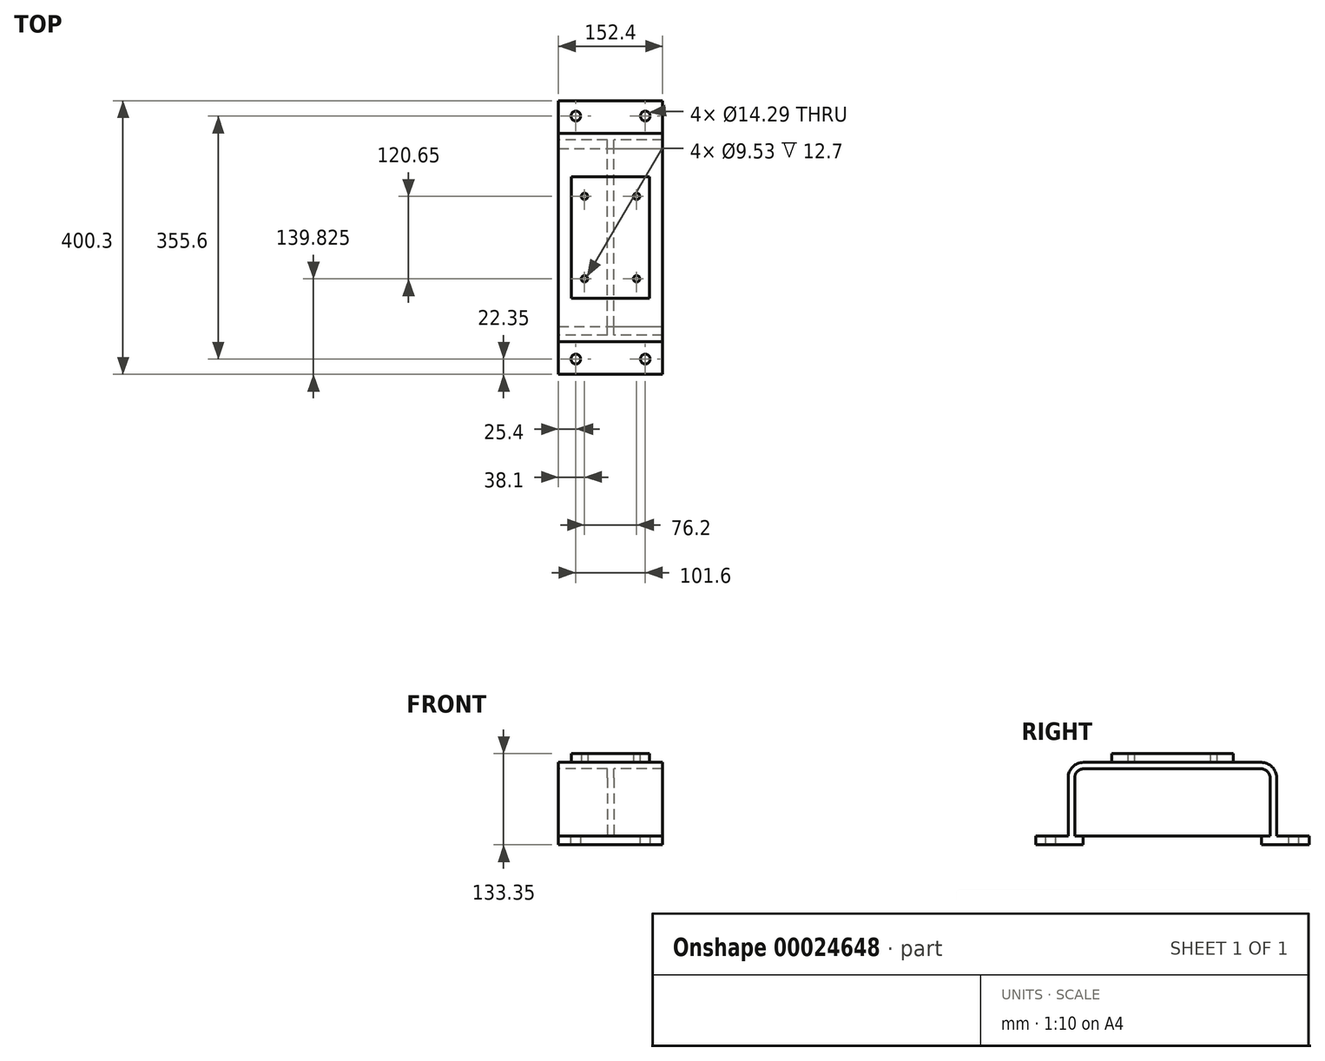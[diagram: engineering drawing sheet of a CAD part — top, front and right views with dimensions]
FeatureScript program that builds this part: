
annotation { "Feature Type Name" : "Feature", "Feature Type Description" : "" }
export const myFeature = defineFeature(function(context is Context, id is Id, definition is map)
    precondition{}
    {
        {
            var Q0;
            Q0=qCreatedBy(makeId("Top.planeOp"),FACE);
            var sketch = newSketch(context, id + "F0", { "sketchPlane" : qUnion([Q0])});
            skLineSegment(sketch, "E0", {"start": v(-115.53, 0) * mm, "end": v(98.36, 0) * mm, "construction": true});
            skLineSegment(sketch, "E1", {"start": v(0, 105.7) * mm, "end": v(0, -103.2) * mm, "construction": true});
            skLineSegment(sketch, "E2.0", {"start": v(-76.2, 105.7) * mm, "end": v(-76.2, -200.15) * mm, "construction": true});
            skLineSegment(sketch, "E3.0", {"start": v(-115.53, -200.15) * mm, "end": v(98.36, -200.15) * mm, "construction": true});
            skLineSegment(sketch, "E4.bottom", {"start": v(-76.2, -200.15) * mm, "end": v(76.2, -200.15) * mm});
            skLineSegment(sketch, "E4.top", {"start": v(-76.2, -130.3) * mm, "end": v(76.2, -130.3) * mm});
            skLineSegment(sketch, "E4.left", {"start": v(-76.2, -200.15) * mm, "end": v(-76.2, -130.3) * mm});
            skLineSegment(sketch, "E4.right", {"start": v(76.2, -200.15) * mm, "end": v(76.2, -130.3) * mm});
            skLineSegment(sketch, "E5.0", {"start": v(-115.53, -177.8) * mm, "end": v(98.36, -177.8) * mm, "construction": true});
            skLineSegment(sketch, "E6", {"start": v(0, -130.3) * mm, "end": v(0, -200.15) * mm, "construction": true});
            skLineSegment(sketch, "E7.0", {"start": v(-50.8, -130.3) * mm, "end": v(-50.8, -200.15) * mm, "construction": true});
            skCircle(sketch, "E8", {"center": v(-50.8, -177.8) * mm, "radius": 7.14 * mm});
            skCircle(sketch, "E9.MirrorC", {"center": v(50.8, -177.8) * mm, "radius": 7.14 * mm});
            skCircle(sketch, "E10.MirrorC", {"center": v(50.8, 177.8) * mm, "radius": 7.14 * mm});
            skCircle(sketch, "E11.MirrorC", {"center": v(-50.8, 177.8) * mm, "radius": 7.14 * mm});
            skLineSegment(sketch, "E12.MirrorCS", {"start": v(0, 130.3) * mm, "end": v(0, 200.15) * mm, "construction": true});
            skLineSegment(sketch, "E13.MirrorCS", {"start": v(-50.8, 130.3) * mm, "end": v(-50.8, 200.15) * mm, "construction": true});
            skLineSegment(sketch, "E14.MirrorCS", {"start": v(-76.2, 200.15) * mm, "end": v(76.2, 200.15) * mm});
            skLineSegment(sketch, "E15.MirrorCS", {"start": v(-76.2, 130.3) * mm, "end": v(76.2, 130.3) * mm});
            skLineSegment(sketch, "E16.MirrorCS", {"start": v(-76.2, 200.15) * mm, "end": v(-76.2, 130.3) * mm});
            skLineSegment(sketch, "E17.MirrorCS", {"start": v(76.2, 200.15) * mm, "end": v(76.2, 130.3) * mm});
            skSolve(sketch);
        }
        {
            var Q0;
            Q0 = qSketchRegion(id + "F0", true);
            extrude(context, id + "F1", {"entities" : qUnion([Q0]), "oppositeDirection" : true, "depth" : 12.7 * mm});
        }
        {
            var Q0;
            Q0=qCreatedBy(makeId("Right.planeOp"),FACE);
            var sketch = newSketch(context, id + "F2", { "sketchPlane" : qUnion([Q0])});
            skLineSegment(sketch, "E18", {"start": v(0, 198.33) * mm, "end": v(0, -186.22) * mm, "construction": true});
            skLineSegment(sketch, "E19", {"start": v(0, 0) * mm, "end": v(-335.1, 0) * mm, "construction": true});
            skLineSegment(sketch, "E20.0", {"start": v(-152.4, 85.6) * mm, "end": v(-152.4, 0) * mm});
            skLineSegment(sketch, "E21.0", {"start": v(0, 107.95) * mm, "end": v(-130.05, 107.95) * mm});
            skPoint(sketch, "E22.visualSharp", {"position": v(-152.4, 107.95) * mm});
            skArc(sketch, "E22.filletArc", {"start": v(-130.05, 107.95) * mm, "mid": v(-145.85, 101.4) * mm, "end": v(-152.4, 85.6) * mm});
            skLineSegment(sketch, "E23.0", {"start": v(-142.87, 85.6) * mm, "end": v(-142.87, 0) * mm});
            skArc(sketch, "E23.1", {"start": v(-130.05, 98.43) * mm, "mid": v(-139.12, 94.67) * mm, "end": v(-142.87, 85.6) * mm});
            skLineSegment(sketch, "E23.2", {"start": v(0, 98.43) * mm, "end": v(-130.05, 98.42) * mm});
            skLineSegment(sketch, "E24", {"start": v(-152.4, 0) * mm, "end": v(-142.87, 0) * mm});
            skLineSegment(sketch, "E25.MirrorCS", {"start": v(152.4, 0) * mm, "end": v(142.87, 0) * mm});
            skArc(sketch, "E26.MirrorCS", {"start": v(130.05, 98.43) * mm, "mid": v(139.12, 94.67) * mm, "end": v(142.87, 85.6) * mm});
            skLineSegment(sketch, "E27.MirrorCS", {"start": v(142.87, 85.6) * mm, "end": v(142.87, 0) * mm});
            skArc(sketch, "E28.MirrorCS", {"start": v(130.05, 107.95) * mm, "mid": v(145.85, 101.4) * mm, "end": v(152.4, 85.6) * mm});
            skLineSegment(sketch, "E29.MirrorCS", {"start": v(0, 107.95) * mm, "end": v(130.05, 107.95) * mm});
            skLineSegment(sketch, "E30.MirrorCS", {"start": v(152.4, 85.6) * mm, "end": v(152.4, 0) * mm});
            skPoint(sketch, "E31.MirrorP", {"position": v(152.4, 107.95) * mm});
            skLineSegment(sketch, "E32.MirrorCS", {"start": v(0, 98.43) * mm, "end": v(130.05, 98.42) * mm});
            skSolve(sketch);
        }
        {
            var Q0;
            Q0 = qSketchRegion(id + "F2", true);
            extrude(context, id + "F3", {"entities" : qUnion([Q0]), "endBound" : BoundingType.SYMMETRIC, "depth" : 152.4 * mm});
        }
        {
            var Q0;
            Q0=qCreatedBy(makeId("Front.planeOp"),FACE);
            var sketch = newSketch(context, id + "F4", { "sketchPlane" : qUnion([Q0])});
            skLineSegment(sketch, "E33", {"start": v(0, 0) * mm, "end": v(0, 134.5) * mm, "construction": true});
            skLineSegment(sketch, "E34.0", {"start": v(-4.76, 0) * mm, "end": v(-4.76, 98.42) * mm});
            skLineSegment(sketch, "E35.0", {"start": v(76.2, 98.42) * mm, "end": v(-76.2, 98.42) * mm});
            skLineSegment(sketch, "E36.MirrorCS", {"start": v(4.76, 0) * mm, "end": v(4.76, 98.42) * mm});
            skLineSegment(sketch, "E37.0", {"start": v(-76.2, 0) * mm, "end": v(76.2, 0) * mm});
            skSolve(sketch);
        }
        {
            var Q0;
            Q0 = qSketchRegion(id + "F4", true);
            var Q1;
            Q1=makeQuery(id+"F3.opExtrude","SWEPT_FACE",FACE,{"disambiguationData":[OSD([sQuery(id+"F2.wireOp",EDGE,"E23.0")])]});
            var Q2;
            Q2=makeQuery(id+"F3.opExtrude","SWEPT_FACE",FACE,{"disambiguationData":[OSD([sQuery(id+"F2.wireOp",EDGE,"E27.MirrorCS")])]});
            extrude(context, id + "F5", {"entities" : qUnion([Q0]), "endBound" : BoundingType.UP_TO_SURFACE, "endBoundEntityFace" : qUnion([Q1]), "depth" : 25.4 * mm, "hasSecondDirection" : true, "secondDirectionBound" : SecondDirectionBoundingType.UP_TO_SURFACE, "secondDirectionOppositeDirection" : true, "secondDirectionBoundEntityFace" : qUnion([Q2]), "secondDirectionDepth" : 25.4 * mm});
        }
        {
            var Q0;
            Q0=makeQuery(id+"F3.opExtrude","SWEPT_BODY",BODY,{"disambiguationData":[OSD([sQuery(id+"F2.wireOp",EDGE,"E20.0"),sQuery(id+"F2.wireOp",EDGE,"E21.0"),sQuery(id+"F2.wireOp",EDGE,"E22.filletArc"),sQuery(id+"F2.wireOp",EDGE,"E23.0"),sQuery(id+"F2.wireOp",EDGE,"E23.1"),sQuery(id+"F2.wireOp",EDGE,"E23.2"),sQuery(id+"F2.wireOp",EDGE,"E24"),sQuery(id+"F2.wireOp",EDGE,"E25.MirrorCS"),sQuery(id+"F2.wireOp",EDGE,"E26.MirrorCS"),sQuery(id+"F2.wireOp",EDGE,"E27.MirrorCS"),sQuery(id+"F2.wireOp",EDGE,"E28.MirrorCS"),sQuery(id+"F2.wireOp",EDGE,"E29.MirrorCS"),sQuery(id+"F2.wireOp",EDGE,"E30.MirrorCS"),sQuery(id+"F2.wireOp",EDGE,"E32.MirrorCS")])]});
            var Q1;
            Q1=makeQuery(id+"F1.opExtrude","SWEPT_BODY",BODY,{"disambiguationData":[OSD([sQuery(id+"F0.wireOp",EDGE,"E4.bottom"),sQuery(id+"F0.wireOp",EDGE,"E4.top"),sQuery(id+"F0.wireOp",EDGE,"E4.left"),sQuery(id+"F0.wireOp",EDGE,"E4.right"),sQuery(id+"F0.wireOp",EDGE,"E8"),sQuery(id+"F0.wireOp",EDGE,"E9.MirrorC")])]});
            var Q2;
            Q2=makeQuery(id+"F1.opExtrude","SWEPT_BODY",BODY,{"disambiguationData":[OSD([sQuery(id+"F0.wireOp",EDGE,"E10.MirrorC"),sQuery(id+"F0.wireOp",EDGE,"E11.MirrorC"),sQuery(id+"F0.wireOp",EDGE,"E14.MirrorCS"),sQuery(id+"F0.wireOp",EDGE,"E15.MirrorCS"),sQuery(id+"F0.wireOp",EDGE,"E16.MirrorCS"),sQuery(id+"F0.wireOp",EDGE,"E17.MirrorCS")])]});
            var Q3;
            Q3=makeQuery(id+"F5.opExtrude","SWEPT_BODY",BODY,{"disambiguationData":[OSD([sQuery(id+"F4.wireOp",EDGE,"E34.0"),sQuery(id+"F4.wireOp",EDGE,"E35.0"),sQuery(id+"F4.wireOp",EDGE,"E36.MirrorCS"),sQuery(id+"F4.wireOp",EDGE,"E37.0")])]});
            booleanBodies(context, id + "F6", {"operationType" : BooleanOperationType.UNION, "tools" : qUnion([Q0, Q1, Q2, Q3])});
        }
        {
            var Q0;
            Q0=makeQuery(id+"F3.opExtrude","SWEPT_FACE",FACE,{"disambiguationData":[OSD([sQuery(id+"F2.wireOp",EDGE,"E21.0"),sQuery(id+"F2.wireOp",EDGE,"E29.MirrorCS")])]});
            var sketch = newSketch(context, id + "F7", { "sketchPlane" : qUnion([Q0])});
            skLineSegment(sketch, "E38.0", {"start": v(-76.2, -200.15) * mm, "end": v(76.2, -200.15) * mm, "construction": true});
            skLineSegment(sketch, "E39.0", {"start": v(-76.2, 200.15) * mm, "end": v(76.2, 200.15) * mm, "construction": true});
            skLineSegment(sketch, "E40", {"start": v(0, -200.15) * mm, "end": v(0, 200.15) * mm, "construction": true});
            skLineSegment(sketch, "E41", {"start": v(-76.2, 0) * mm, "end": v(76.2, 0) * mm, "construction": true});
            skLineSegment(sketch, "E42.0", {"start": v(-76.2, -88.9) * mm, "end": v(76.2, -88.9) * mm, "construction": true});
            skLineSegment(sketch, "E43.0", {"start": v(57.15, -200.15) * mm, "end": v(57.15, 200.15) * mm, "construction": true});
            skLineSegment(sketch, "E44.bottom", {"start": v(57.15, -88.9) * mm, "end": v(-57.15, -88.9) * mm});
            skLineSegment(sketch, "E44.top", {"start": v(57.15, 88.9) * mm, "end": v(-57.15, 88.9) * mm});
            skLineSegment(sketch, "E44.left", {"start": v(57.15, -88.9) * mm, "end": v(57.15, 88.9) * mm});
            skLineSegment(sketch, "E44.right", {"start": v(-57.15, -88.9) * mm, "end": v(-57.15, 88.9) * mm});
            skLineSegment(sketch, "E45.0", {"start": v(38.1, -200.15) * mm, "end": v(38.1, 200.15) * mm, "construction": true});
            skLineSegment(sketch, "E46.0", {"start": v(-76.2, -60.33) * mm, "end": v(76.2, -60.33) * mm, "construction": true});
            skCircle(sketch, "E47", {"center": v(38.1, -60.33) * mm, "radius": 4.76 * mm});
            skCircle(sketch, "E48.MirrorC", {"center": v(38.1, 60.33) * mm, "radius": 4.76 * mm});
            skCircle(sketch, "E49.MirrorC", {"center": v(-38.1, -60.33) * mm, "radius": 4.76 * mm});
            skCircle(sketch, "E50.MirrorC", {"center": v(-38.1, 60.33) * mm, "radius": 4.76 * mm});
            skSolve(sketch);
        }
        {
            var Q0;
            Q0 = qSketchRegion(id + "F7", true);
            extrude(context, id + "F8", {"entities" : qUnion([Q0]), "operationType" : NewBodyOperationType.ADD, "depth" : 12.7 * mm});
        }
    });
